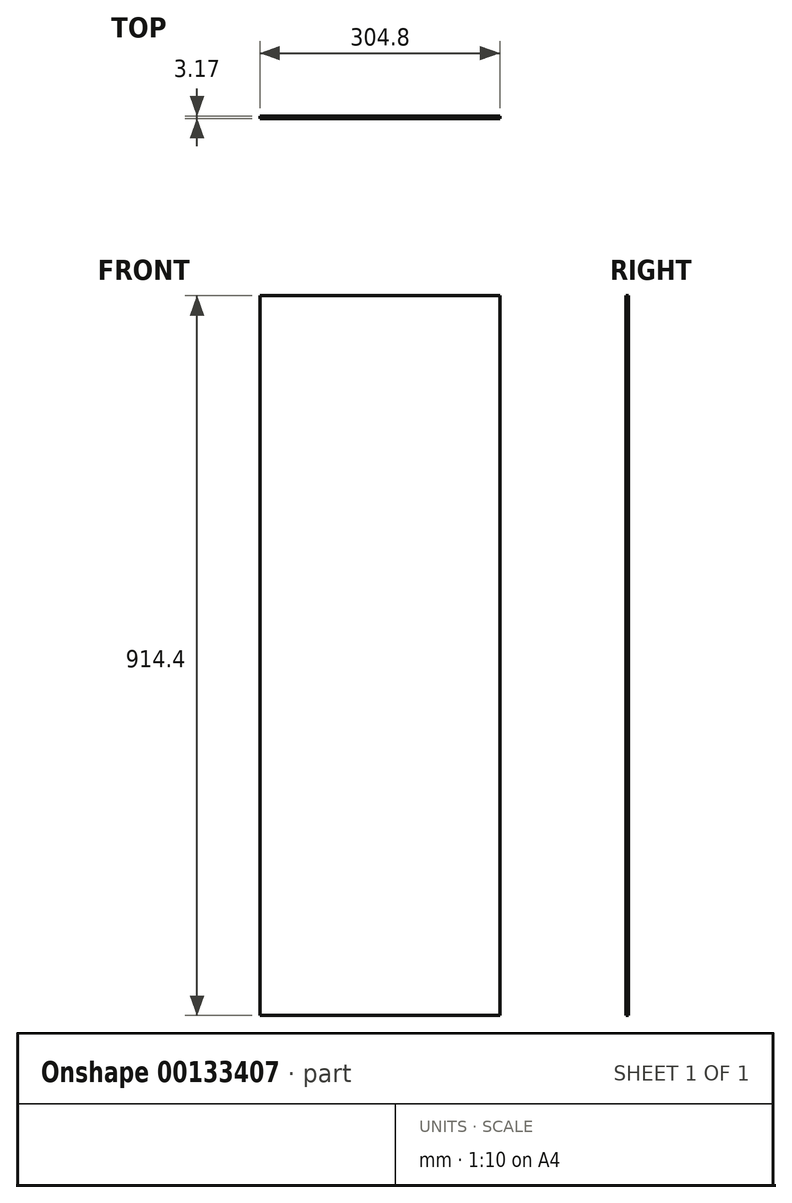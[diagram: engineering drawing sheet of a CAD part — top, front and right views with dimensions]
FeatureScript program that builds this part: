
annotation { "Feature Type Name" : "Feature", "Feature Type Description" : "" }
export const myFeature = defineFeature(function(context is Context, id is Id, definition is map)
    precondition{}
    {
        {
            var Q0;
            Q0=qCreatedBy(makeId("Front.planeOp"),FACE);
            var sketch = newSketch(context, id + "F0", { "sketchPlane" : qUnion([Q0])});
            skLineSegment(sketch, "E0.bottom", {"start": v(-152.4, 457.2) * mm, "end": v(152.4, 457.2) * mm});
            skLineSegment(sketch, "E0.top", {"start": v(-152.4, -457.2) * mm, "end": v(152.4, -457.2) * mm});
            skLineSegment(sketch, "E0.left", {"start": v(-152.4, 457.2) * mm, "end": v(-152.4, -457.2) * mm});
            skLineSegment(sketch, "E0.right", {"start": v(152.4, 457.2) * mm, "end": v(152.4, -457.2) * mm});
            skPoint(sketch, "E0.middle", {"position": v(0, 0) * mm});
            skSolve(sketch);
        }
        {
            var Q0;
            Q0=qSketchRegion(id+"F0",true);
            extrude(context, id + "F1", {"entities" : qUnion([Q0]), "depth" : 3.17 * mm});
        }
    });
